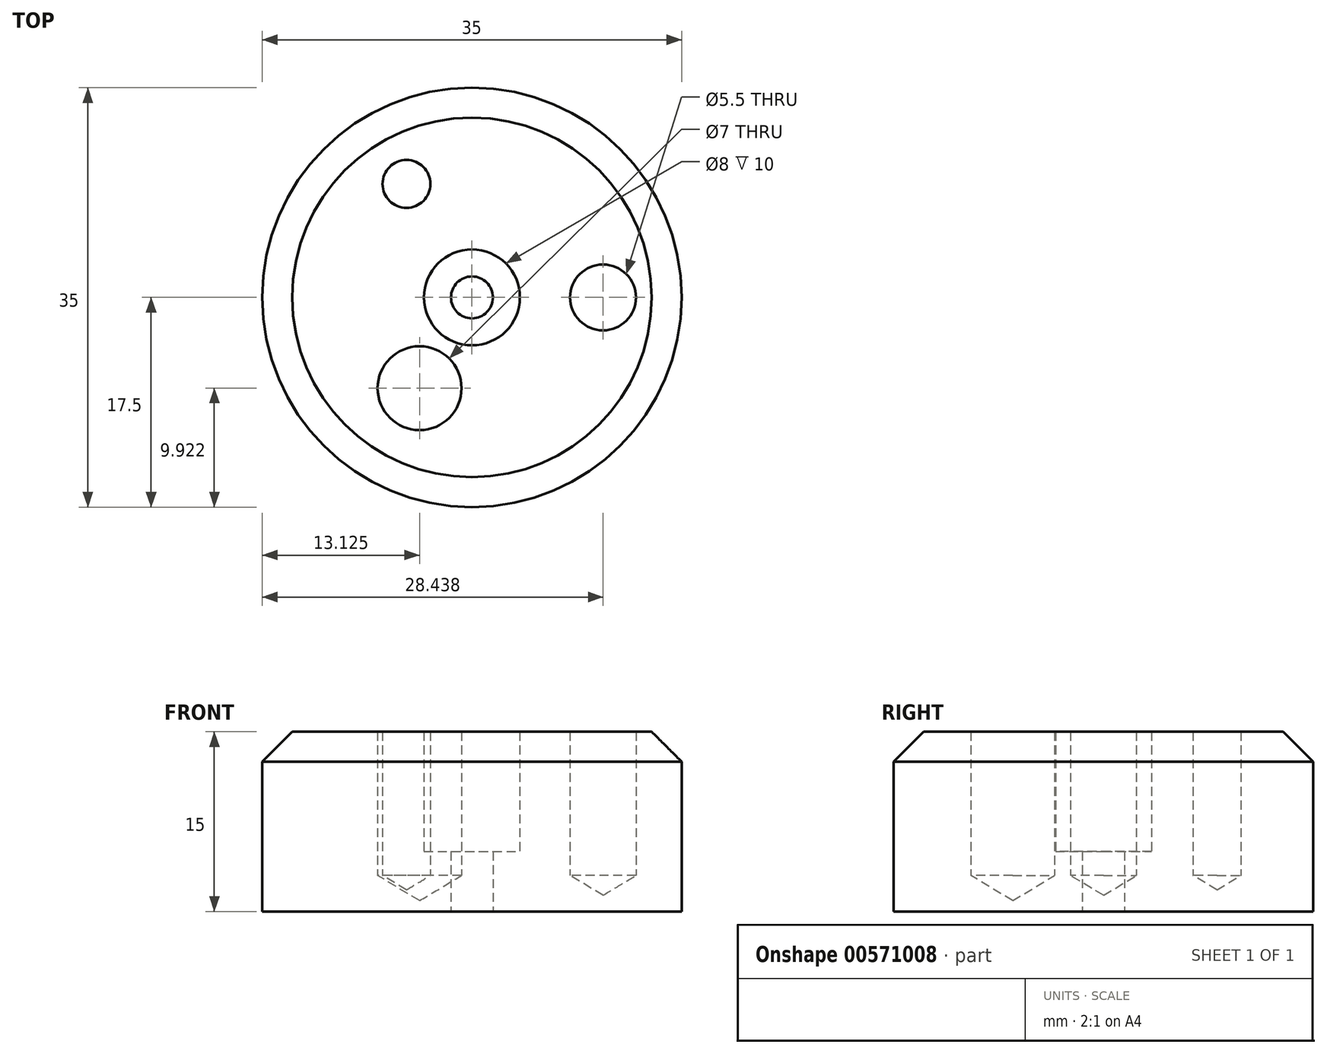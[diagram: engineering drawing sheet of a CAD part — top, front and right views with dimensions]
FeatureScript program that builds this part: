
annotation { "Feature Type Name" : "Feature", "Feature Type Description" : "" }
export const myFeature = defineFeature(function(context is Context, id is Id, definition is map)
    precondition{}
    {
        {
            var Q0;
            Q0=qCreatedBy(makeId("Top.planeOp"),FACE);
            var sketch = newSketch(context, id + "F0", { "sketchPlane" : qUnion([Q0])});
            skCircle(sketch, "E0.cCircle", {"center": v(0, 0) * mm, "radius": 17.5 * mm});
            skPoint(sketch, "E0.0.midPoint", {"position": v(17.5, 0) * mm});
            skLineSegment(sketch, "E1", {"start": v(8.75, 0) * mm, "end": v(13.13, 0) * mm, "construction": true});
            skPoint(sketch, "E2", {"position": v(8.75, 0) * mm});
            skPoint(sketch, "E3", {"position": v(13.13, 0) * mm});
            skPoint(sketch, "E4", {"position": v(10.94, 0) * mm});
            skPoint(sketch, "E5.1.0", {"position": v(-5.47, 9.47) * mm});
            skPoint(sketch, "E5.1.1", {"position": v(-4.37, 7.58) * mm});
            skPoint(sketch, "E5.1.2", {"position": v(-6.56, 11.37) * mm});
            skPoint(sketch, "E5.2.0", {"position": v(-5.47, -9.47) * mm});
            skPoint(sketch, "E5.2.1", {"position": v(-4.38, -7.58) * mm});
            skPoint(sketch, "E5.2.2", {"position": v(-6.56, -11.37) * mm});
            skSolve(sketch);
        }
        {
            var Q0;
            Q0=makeQuery(id+"F0.imprint","IMPRINT",FACE,{"disambiguationData":[TD([[makeQuery(id+"F0.imprint","IMPRINT",EDGE,{"derivedFrom":sQuery(id+"F0.wireOp",EDGE,"E0.cCircle")}),1.0]])]});
            extrude(context, id + "F1", {"entities" : qUnion([Q0]), "flatOperationType" : FlatOperationType.REMOVE, "oppositeDirection" : true, "depth" : 15 * mm, "offsetDistance" : 25 * mm, "domain" : OperationDomain.MODEL});
        }
        {
            var Q0;
            Q0=sQuery(id+"F0.wireOp",VERTEX,"E4");
            var Q1;
            Q1=makeQuery(id+"F1.opExtrude","SWEPT_BODY",BODY,{"disambiguationData":[OSD([sQuery(id+"F0.wireOp",EDGE,"E0.cCircle")])]});
            hole(context, id + "F2", {"style" : HoleStyle.SIMPLE, "endStyle" : HoleEndStyle.BLIND, "holeDiameter" : 5.5 * mm, "majorDiameter" : 5 * mm, "holeDepth" : 12 * mm, "isTappedThrough" : true, "tappedDepth" : 26.25 * mm, "tapClearance" : 3, "locations" : qUnion([Q0]), "scope" : qUnion([Q1]), "startStyle" : HoleStartStyle.PART});
        }
        {
            var Q0;
            Q0=sQuery(id+"F0.wireOp",VERTEX,"E5.2.1");
            var Q1;
            Q1=makeQuery(id+"F1.opExtrude","SWEPT_BODY",BODY,{"disambiguationData":[OSD([sQuery(id+"F0.wireOp",EDGE,"E0.cCircle")])]});
            hole(context, id + "F3", {"style" : HoleStyle.SIMPLE, "endStyle" : HoleEndStyle.BLIND, "holeDiameter" : 7 * mm, "majorDiameter" : 5 * mm, "holeDepth" : 12 * mm, "isTappedThrough" : true, "tappedDepth" : 26.25 * mm, "tapClearance" : 3, "locations" : qUnion([Q0]), "scope" : qUnion([Q1]), "startStyle" : HoleStartStyle.PART});
        }
        {
            var Q0;
            Q0=sQuery(id+"F0.wireOp",VERTEX,"E5.1.0");
            var Q1;
            Q1=makeQuery(id+"F1.opExtrude","SWEPT_BODY",BODY,{"disambiguationData":[OSD([sQuery(id+"F0.wireOp",EDGE,"E0.cCircle")])]});
            hole(context, id + "F4", {"style" : HoleStyle.SIMPLE, "endStyle" : HoleEndStyle.BLIND, "holeDiameter" : 4 * mm, "majorDiameter" : 5 * mm, "holeDepth" : 12 * mm, "isTappedThrough" : true, "tappedDepth" : 26.25 * mm, "tapClearance" : 3, "locations" : qUnion([Q0]), "scope" : qUnion([Q1]), "startStyle" : HoleStartStyle.PART});
        }
        {
            var Q0;
            Q0=sQuery(id+"F0.wireOp",VERTEX,"E0.cCircle.center");
            var Q1;
            Q1=makeQuery(id+"F1.opExtrude","SWEPT_BODY",BODY,{"disambiguationData":[OSD([sQuery(id+"F0.wireOp",EDGE,"E0.cCircle")])]});
            hole(context, id + "F5", {"style" : HoleStyle.C_BORE, "endStyle" : HoleEndStyle.THROUGH, "holeDiameter" : 3.5 * mm, "cBoreDiameter" : 8 * mm, "cBoreDepth" : 10 * mm, "majorDiameter" : 5 * mm, "isTappedThrough" : true, "tappedDepth" : 26.25 * mm, "tapClearance" : 3, "locations" : qUnion([Q0]), "scope" : qUnion([Q1]), "startStyle" : HoleStartStyle.PART});
        }
        {
            var Q0;
            Q0=makeQuery(id+"F1.opExtrude","CAP_EDGE",EDGE,{"disambiguationData":[OSD([sQuery(id+"F0.wireOp",EDGE,"E0.cCircle")])],"isStart":true});
            chamfer(context, id + "F6", {"entities" : qUnion([Q0]), "width" : 2.5 * mm, "tangentPropagation" : true});
        }
    });
